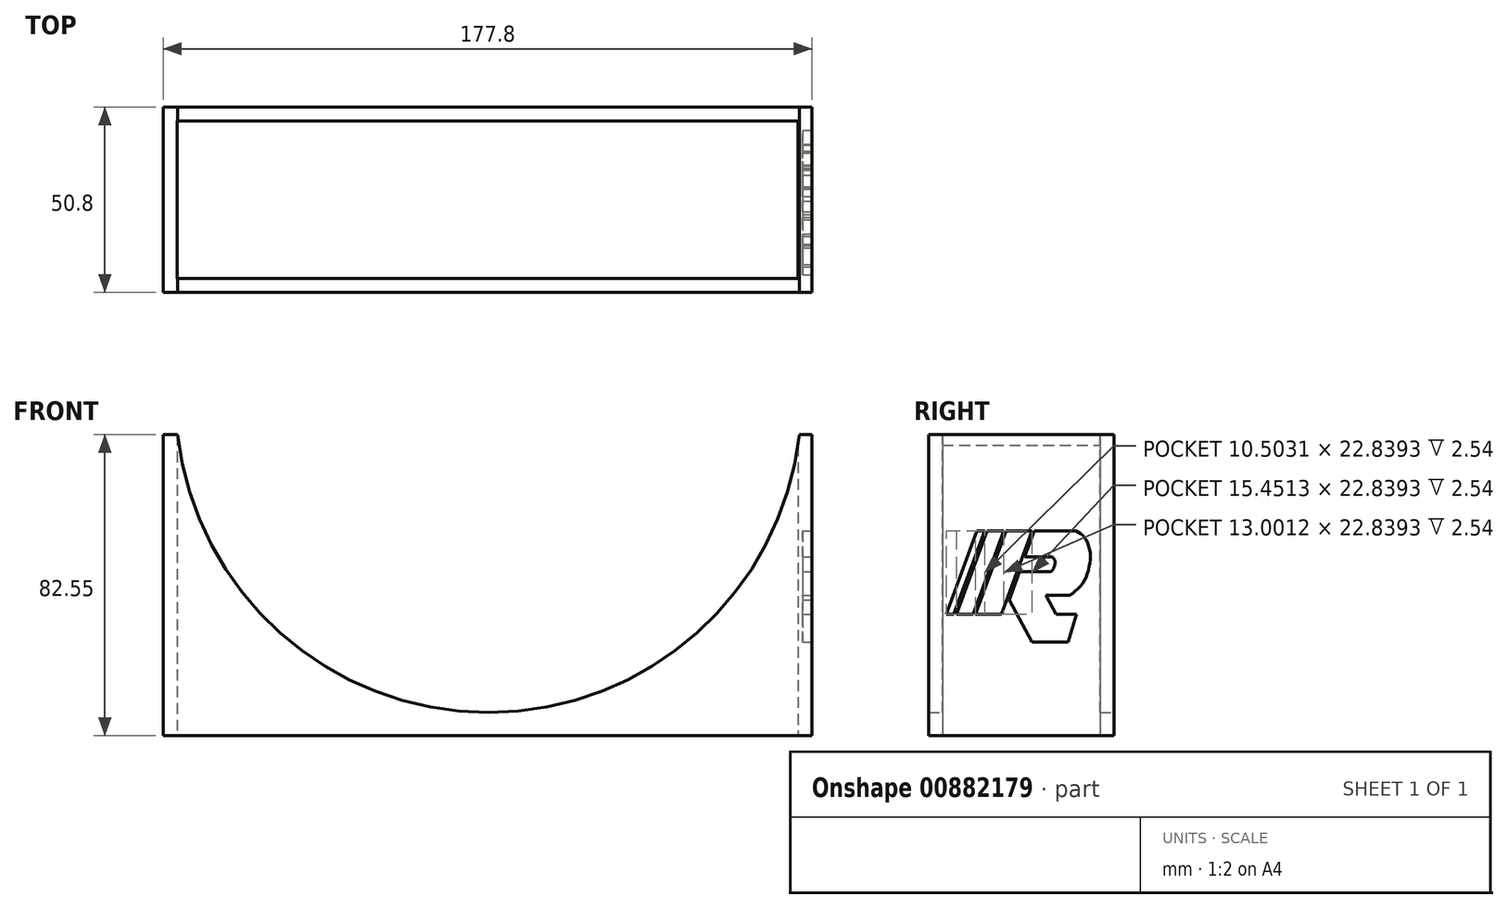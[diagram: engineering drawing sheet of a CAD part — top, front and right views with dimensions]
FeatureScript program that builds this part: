
annotation { "Feature Type Name" : "Feature", "Feature Type Description" : "" }
export const myFeature = defineFeature(function(context is Context, id is Id, definition is map)
    precondition{}
    {
        {
            var Q0;
            Q0=qCreatedBy(makeId("Front.planeOp"),FACE);
            var sketch = newSketch(context, id + "F0", { "sketchPlane" : qUnion([Q0])});
            skLineSegment(sketch, "E0.top", {"start": v(-89.18, 0) * mm, "end": v(88.62, 0) * mm});
            skLineSegment(sketch, "E0.left", {"start": v(-89.18, 82.55) * mm, "end": v(-89.18, 0) * mm});
            skLineSegment(sketch, "E0.right", {"start": v(88.62, 82.55) * mm, "end": v(88.62, 0) * mm});
            skArc(sketch, "E1", {"start": v(-85.2, 82.55) * mm, "mid": v(0, 6.35) * mm, "end": v(85.2, 82.55) * mm});
            skLineSegment(sketch, "E2", {"start": v(-89.18, 82.55) * mm, "end": v(-85.2, 82.55) * mm});
            skLineSegment(sketch, "E3.trimOffspring", {"start": v(85.2, 82.55) * mm, "end": v(88.62, 82.55) * mm});
            skSolve(sketch);
        }
        {
            var Q0;
            Q0 = qSketchRegion(id + "F0", true);
            extrude(context, id + "F1", {"entities" : qUnion([Q0]), "depth" : 50.8 * mm, "offsetDistance" : 25.4 * mm});
        }
        {
            var Q0;
            Q0=makeQuery(id+"F1.opExtrude","SWEPT_FACE",FACE,{"disambiguationData":[OSD([sQuery(id+"F0.wireOp",EDGE,"E0.right")])]});
            var sketch = newSketch(context, id + "F2", { "sketchPlane" : qUnion([Q0])});
            skLineSegment(sketch, "E4", {"start": v(-45.97, 33.28) * mm, "end": v(-37.56, 56.12) * mm});
            skLineSegment(sketch, "E5", {"start": v(-30.88, 33.28) * mm, "end": v(-37.93, 33.28) * mm});
            skLineSegment(sketch, "E6", {"start": v(-35.46, 56.12) * mm, "end": v(-43.87, 33.28) * mm});
            skLineSegment(sketch, "E7", {"start": v(-43.22, 33.28) * mm, "end": v(-34.81, 56.12) * mm});
            skLineSegment(sketch, "E8", {"start": v(-30.21, 56.12) * mm, "end": v(-38.62, 33.28) * mm});
            skLineSegment(sketch, "E9", {"start": v(-37.93, 33.28) * mm, "end": v(-29.52, 56.12) * mm});
            skLineSegment(sketch, "E10", {"start": v(-22.47, 56.12) * mm, "end": v(-30.88, 33.28) * mm});
            skLineSegment(sketch, "E11", {"start": v(-24.46, 49) * mm, "end": v(-21.84, 56.12) * mm});
            skLineSegment(sketch, "E12", {"start": v(-24.46, 49) * mm, "end": v(-16.82, 49) * mm});
            skLineSegment(sketch, "E13", {"start": v(-17.23, 45) * mm, "end": v(-25.85, 45) * mm});
            skLineSegment(sketch, "E14", {"start": v(-25.85, 45) * mm, "end": v(-28.7, 37.22) * mm});
            skLineSegment(sketch, "E15", {"start": v(-28.7, 37.22) * mm, "end": v(-22.4, 25.64) * mm});
            skLineSegment(sketch, "E16", {"start": v(-22.4, 25.64) * mm, "end": v(-12.54, 25.64) * mm});
            skLineSegment(sketch, "E17", {"start": v(-12.54, 25.64) * mm, "end": v(-10.2, 33.33) * mm});
            skLineSegment(sketch, "E18", {"start": v(-10.2, 33.33) * mm, "end": v(-15.9, 33.33) * mm});
            skLineSegment(sketch, "E19", {"start": v(-15.9, 33.33) * mm, "end": v(-18.7, 38.47) * mm});
            skLineSegment(sketch, "E20", {"start": v(-18.7, 38.47) * mm, "end": v(-12.1, 38.47) * mm});
            skFitSpline(sketch, "E21", {"points": [v(-10.42, 56.12) * mm, v(-8.7, 55.07) * mm, v(-7.4, 53.26) * mm, v(-6.5, 50.2) * mm, v(-6.67, 46.94) * mm, v(-7.66, 43.4) * mm, v(-9.6, 40.52) * mm, v(-12.1, 38.47) * mm], "startDerivative": vector(15.57, -7.81) * mm, "endDerivative": vector(-17.57, -12.75) * mm});
            skLineSegment(sketch, "E22.trimOffspring", {"start": v(-35.46, 56.12) * mm, "end": v(-37.56, 56.12) * mm});
            skLineSegment(sketch, "E23.trimOffspring", {"start": v(-30.21, 56.12) * mm, "end": v(-34.81, 56.12) * mm});
            skLineSegment(sketch, "E24.trimOffspring", {"start": v(-22.47, 56.12) * mm, "end": v(-29.52, 56.12) * mm});
            skLineSegment(sketch, "E25.trimOffspring", {"start": v(-10.42, 56.12) * mm, "end": v(-21.84, 56.12) * mm});
            skLineSegment(sketch, "E26.trimOffspring", {"start": v(-38.62, 33.28) * mm, "end": v(-43.22, 33.28) * mm});
            skLineSegment(sketch, "E27.trimOffspring", {"start": v(-43.87, 33.28) * mm, "end": v(-45.97, 33.28) * mm});
            skFitSpline(sketch, "E28", {"points": [v(-16.82, 49) * mm, v(-16.2, 48.07) * mm, v(-16.23, 46.76) * mm, v(-16.82, 45.39) * mm, v(-17.23, 45) * mm], "startDerivative": vector(3.01, -3.4) * mm, "endDerivative": vector(-2.27, -1.67) * mm});
            skSolve(sketch);
        }
        {
            var Q0;
            Q0 = qSketchRegion(id + "F2", true);
            extrude(context, id + "F3", {"entities" : qUnion([Q0]), "operationType" : NewBodyOperationType.REMOVE, "oppositeDirection" : true, "depth" : 2.54 * mm, "offsetDistance" : 25.4 * mm});
        }
        {
            var Q0;
            Q0=makeQuery(id+"F1.opExtrude","SWEPT_FACE",FACE,{"disambiguationData":[OSD([sQuery(id+"F0.wireOp",EDGE,"E0.top")])]});
            var sketch = newSketch(context, id + "F4", { "sketchPlane" : qUnion([Q0])});
            skLineSegment(sketch, "E29.bottom", {"start": v(-85.37, 47) * mm, "end": v(84.81, 47) * mm});
            skLineSegment(sketch, "E29.top", {"start": v(-85.37, 3.81) * mm, "end": v(84.81, 3.81) * mm});
            skLineSegment(sketch, "E29.left", {"start": v(-85.37, 47) * mm, "end": v(-85.37, 3.81) * mm});
            skLineSegment(sketch, "E29.right", {"start": v(84.81, 47) * mm, "end": v(84.81, 3.81) * mm});
            skSolve(sketch);
        }
        {
            var Q0;
            Q0 = qSketchRegion(id + "F4", true);
            extrude(context, id + "F5", {"entities" : qUnion([Q0]), "operationType" : NewBodyOperationType.REMOVE, "endBound" : BoundingType.THROUGH_ALL, "oppositeDirection" : true, "depth" : 25.4 * mm, "offsetDistance" : 25.4 * mm});
        }
    });
